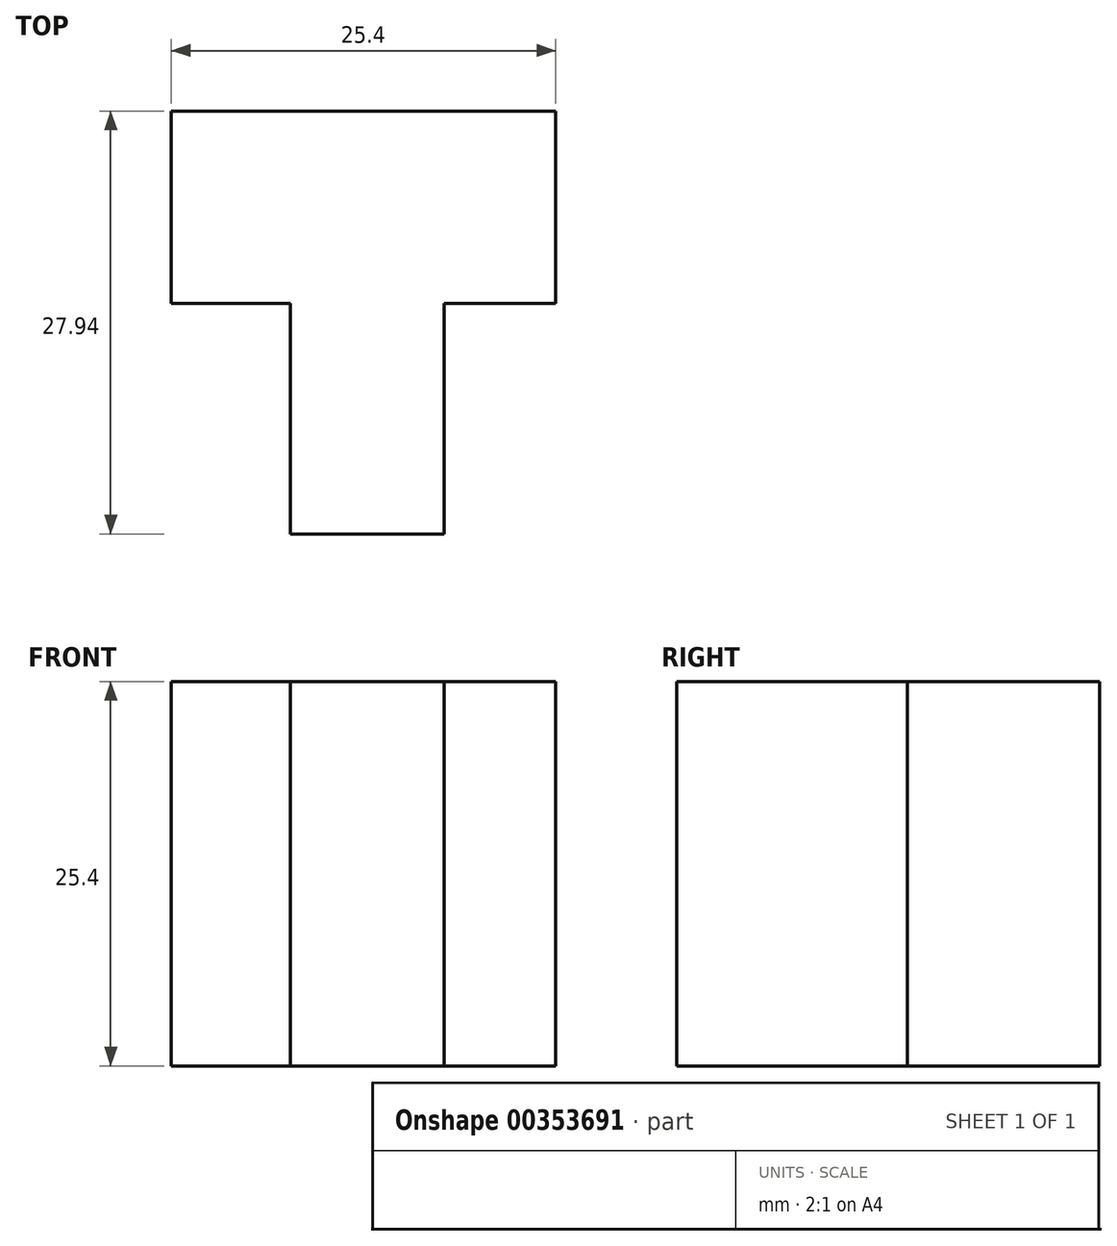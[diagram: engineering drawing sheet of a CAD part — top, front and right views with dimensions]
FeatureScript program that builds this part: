
annotation { "Feature Type Name" : "Feature", "Feature Type Description" : "" }
export const myFeature = defineFeature(function(context is Context, id is Id, definition is map)
    precondition{}
    {
        {
            var Q0;
            Q0=qCreatedBy(makeId("Top.planeOp"),FACE);
            var sketch = newSketch(context, id + "F0", { "sketchPlane" : qUnion([Q0])});
            skLineSegment(sketch, "E0", {"start": v(-6.55, 31.96) * mm, "end": v(18.85, 31.96) * mm});
            skLineSegment(sketch, "E1", {"start": v(18.85, 31.96) * mm, "end": v(18.85, 19.26) * mm});
            skLineSegment(sketch, "E2", {"start": v(-6.55, 31.96) * mm, "end": v(-6.55, 19.26) * mm});
            skLineSegment(sketch, "E3", {"start": v(-6.55, 19.26) * mm, "end": v(1.3, 19.26) * mm});
            skLineSegment(sketch, "E4", {"start": v(1.3, 19.26) * mm, "end": v(1.3, 4.02) * mm});
            skLineSegment(sketch, "E5", {"start": v(1.3, 4.02) * mm, "end": v(11.46, 4.02) * mm});
            skLineSegment(sketch, "E6", {"start": v(11.46, 4.02) * mm, "end": v(11.46, 19.26) * mm});
            skLineSegment(sketch, "E7", {"start": v(11.46, 19.26) * mm, "end": v(18.85, 19.26) * mm});
            skSolve(sketch);
        }
        {
            var Q0;
            Q0 = qSketchRegion(id + "F0", true);
            extrude(context, id + "F1", {"entities" : qUnion([Q0]), "depth" : 25.4 * mm});
        }
    });
